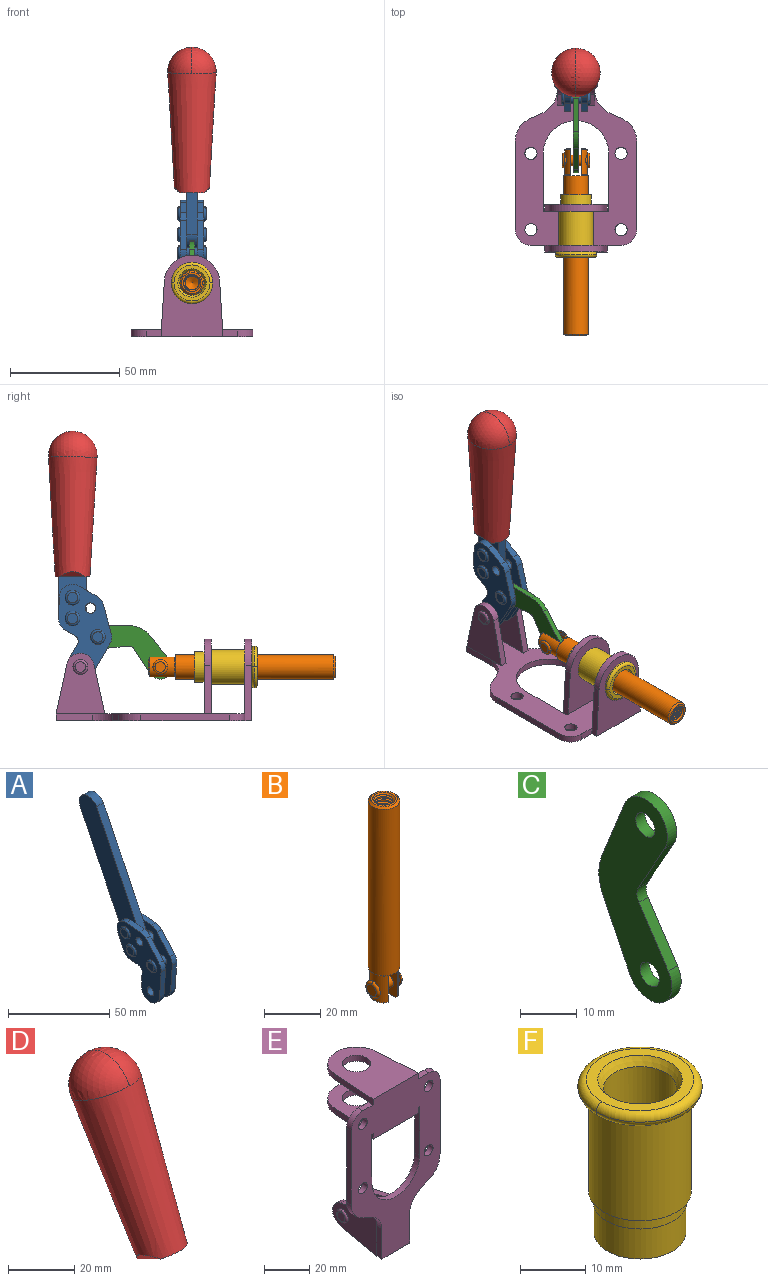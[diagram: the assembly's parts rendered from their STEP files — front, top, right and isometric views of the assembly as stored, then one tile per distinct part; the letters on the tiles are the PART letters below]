
ASSEMBLY  parts=6 mates=6
PART A: 59 faces, bbox 12.9x60.2x99.6 mm
  f0: torus R=2.39mm, axis (-1,0,0), area 14.9mm2, adj f20,f43,f51
  f1: torus R=2.39mm, axis (-1,0,0), area 14.9mm2, adj f19,f42,f51
  f2: torus R=2.39mm, axis (-1,0,0), area 14.9mm2, adj f18,f35,f51
  f3: torus R=2.39mm, axis (-1,0,0), area 14.9mm2, adj f14,f17,f23
  f4: torus R=2.39mm, axis (-1,0,0), area 14.9mm2, adj f13,f16,f23
  f5: torus R=2.39mm, axis (-1,0,0), area 14.9mm2, adj f12,f15,f23
  f6: cylinder r=2.39mm len=4.78mm, axis (1,0,0), area 46.5mm2, adj f48,f50,f51
  f7: cylinder r=2.39mm len=4.78mm, axis (1,0,0), area 46.5mm2, adj f50,f51
  f8: cylinder r=6.35mm len=12.68mm, axis (1,0,0), area 61.8mm2, adj f38,f39,f50,f51
  f9: cylinder r=2.39mm len=4.78mm, axis (-1,0,0), area 70.5mm2, adj f46,f50
  f10: cylinder r=2.39mm len=4.78mm, axis (-1,0,0), area 46.5mm2, adj f23,f45,f46
  f11: cylinder r=2.39mm len=4.78mm, axis (-1,0,0), area 46.5mm2, adj f23,f46
  f12: plane 4.78x4.78mm, normal (1,0,0), area 17.9mm2, adj f5,f15
  f13: plane 4.78x4.78mm, normal (1,0,0), area 17.9mm2, adj f4,f16
  f14: plane 4.78x4.78mm, normal (1,0,0), area 17.9mm2, adj f3,f17
  f15: torus R=2.39mm, axis (-1,0,0), area 14.9mm2, adj f5,f12,f23
  f16: torus R=2.39mm, axis (-1,0,0), area 14.9mm2, adj f4,f13,f23
  f17: torus R=2.39mm, axis (-1,0,0), area 14.9mm2, adj f3,f14,f23
  f18: plane 4.78x4.78mm, normal (-1,0,0), area 17.9mm2, adj f2,f35
  f19: plane 4.78x4.78mm, normal (-1,0,0), area 17.9mm2, adj f1,f42
  f20: plane 4.78x4.78mm, normal (-1,0,0), area 17.9mm2, adj f0,f43
  f21: plane 2.26x0.2mm, normal (1,0,0), area 0.2mm2, adj f31,f44
  f22: plane 2.26x0.2mm, normal (-1,0,0), area 0.2mm2, adj f41,f44
  f23: plane 39.37x30.77mm, normal (1,0,0), area 565.5mm2, adj f3,f4,f5,f10,f11,f15,f16,f17
  f24: cylinder r=6.1mm len=4.15mm, axis (-1,0,0), area 14.7mm2, adj f23,f25,f32,f46
  f25: plane 10.25x9.01mm, normal (0,-0.75,0.66), area 42.3mm2, adj f23,f24,f26,f46
  f26: cylinder r=6.35mm len=4.64mm, axis (-1,0,0), area 15.6mm2, adj f23,f25,f27,f46
  f27: plane 15.84x3.1mm, normal (0,-1,-0.07), area 49.2mm2, adj f23,f26,f28,f46
  f28: cylinder r=6.35mm len=12.68mm, axis (-1,0,0), area 61.8mm2, adj f23,f27,f29,f46
  f29: plane 8.11x3.1mm, normal (0,1,0.07), area 25.2mm2, adj f23,f28,f30,f46
  f30: cylinder r=3.05mm len=3.25mm, axis (-1,0,0), area 14.8mm2, adj f23,f29,f31,f46
  f31: plane 5.99x3.1mm, normal (0,0.07,-1), area 18.6mm2, adj f21,f23,f30,f44,f46
  f32: plane 9.5x3.1mm, normal (0,-0.07,1), area 29.5mm2, adj f23,f24,f33,f46,f47
  f33: cylinder r=6.1mm len=8.63mm, axis (-1,0,0), area 39.1mm2, adj f23,f32,f34,f47
  f34: plane 8.65x3.96mm, normal (0,0.91,-0.42), area 29.5mm2, adj f23,f33,f44,f47
  f35: torus R=2.39mm, axis (-1,0,0), area 14.9mm2, adj f2,f18,f51
  f36: plane 10.25x9.01mm, normal (0,-0.75,0.66), area 42.3mm2, adj f37,f49,f50,f51
  f37: cylinder r=6.35mm len=4.64mm, axis (1,0,0), area 15.6mm2, adj f36,f38,f50,f51
  f38: plane 15.84x3.1mm, normal (0,-1,-0.07), area 49.2mm2, adj f8,f37,f50,f51
  f39: plane 8.11x3.1mm, normal (0,1,0.07), area 25.2mm2, adj f8,f40,f50,f51
  f40: cylinder r=3.05mm len=3.25mm, axis (1,0,0), area 14.8mm2, adj f39,f41,f50,f51
  f41: plane 5.99x3.1mm, normal (0,0.07,-1), area 18.6mm2, adj f22,f40,f44,f50,f51
  f42: torus R=2.39mm, axis (-1,0,0), area 14.9mm2, adj f1,f19,f51
  f43: torus R=2.39mm, axis (-1,0,0), area 14.9mm2, adj f0,f20,f51
  f44: cylinder r=6.35mm len=12.12mm, axis (-1,0,0), area 128.9mm2, adj f21,f22,f23,f31,f34,f41,f46,f47
  f45: plane 2.65x1.35mm, normal (1,0,0), area 1mm2, adj f10,f55
  f46: plane 39.08x20.42mm, normal (-1,0,0), area 412.5mm2, adj f9,f10,f11,f24,f25,f26,f27,f28
  f47: plane 77.62x39.82mm, normal (1,0,0), area 850mm2, adj f32,f33,f34,f44,f53,f54,f55
  f48: plane 2.65x1.35mm, normal (-1,0,0), area 1mm2, adj f6,f55
  f49: cylinder r=6.1mm len=4.15mm, axis (1,0,0), area 14.7mm2, adj f36,f50,f51,f56
  f50: plane 39.08x20.42mm, normal (1,0,0), area 412.5mm2, adj f6,f7,f8,f9,f36,f37,f38,f39
  f51: plane 39.37x30.77mm, normal (-1,0,0), area 565.5mm2, adj f0,f1,f2,f6,f7,f8,f35,f36
  f52: plane 8.65x3.96mm, normal (0,0.91,-0.42), area 29.5mm2, adj f44,f51,f57,f58
  f53: plane 68.49x33.4mm, normal (0,0.9,-0.44), area 358.1mm2, adj f44,f47,f54,f58
  f54: cylinder r=6.35mm len=12.06mm, axis (1,0,0), area 93.7mm2, adj f47,f53,f55,f58
  f55: plane 68.49x33.4mm, normal (0,-0.9,0.44), area 358.1mm2, adj f44,f45,f46,f47,f48,f50,f54,f58
  f56: plane 9.5x3.1mm, normal (0,-0.07,1), area 29.5mm2, adj f49,f50,f51,f57,f58
  f57: cylinder r=6.1mm len=8.63mm, axis (1,0,0), area 39.1mm2, adj f51,f52,f56,f58
  f58: plane 77.62x39.82mm, normal (-1,0,0), area 850mm2, adj f44,f52,f53,f54,f55,f56,f57
PART B: 48 faces, bbox 12.6x11.1x86.1 mm
  f0: torus R=2.41mm, axis (-1,0,0), area 15mm2, adj f30,f32,f34
  f1: torus R=2.41mm, axis (-1,0,0), area 15mm2, adj f29,f31,f33
  f2: cylinder r=5.54mm len=72.39mm, axis (0,0,1), area 2518.5mm2, adj f3,f4,f42,f43
  f3: cone r=5.54mm half-angle=45deg, axis (0,0,1), area 7.6mm2, adj f2,f5,f41
  f4: cone r=5.54mm half-angle=45deg, axis (0,0,-1), area 34.9mm2, adj f2,f39
  f5: cylinder r=5.08mm len=11.48mm, axis (0,0,1), area 108.3mm2, adj f3,f7,f8,f41
  f6: cylinder r=2.41mm len=4.83mm, axis (-1,0,0), area 71.2mm2, adj f40,f41
  f7: cylinder r=2.41mm len=4.83mm, axis (-1,0,0), area 7.6mm2, adj f5,f34
  f8: cone r=5.08mm half-angle=45deg, axis (0,0,1), area 10.6mm2, adj f5,f37,f41
  f9: cone r=3.98mm half-angle=45deg, axis (0,0,1), area 17.6mm2, adj f27,f39,f45,f46,f47
  f10: cylinder r=2.41mm len=4.83mm, axis (-1,0,0), area 7.6mm2, adj f33,f38
  f11: cylinder r=3.2mm len=6.4mm, axis (0,0,1), area 78.4mm2, adj f12,f28,f44,f45,f47
  f12: cylinder r=3.2mm len=6.4mm, axis (0,0,1), area 10.5mm2, adj f11,f13,f45,f47
  f13: cylinder r=3.2mm len=6.4mm, axis (0,0,1), area 10.5mm2, adj f12,f14,f45,f47
  f14: cylinder r=3.2mm len=6.4mm, axis (0,0,1), area 10.5mm2, adj f13,f15,f45,f47
  f15: cylinder r=3.2mm len=6.4mm, axis (0,0,1), area 10.5mm2, adj f14,f16,f45,f47
  f16: cylinder r=3.2mm len=6.4mm, axis (0,0,1), area 10.5mm2, adj f15,f17,f45,f47
  f17: cylinder r=3.2mm len=6.4mm, axis (0,0,1), area 10.5mm2, adj f16,f18,f45,f47
  f18: cylinder r=3.2mm len=6.4mm, axis (0,0,1), area 10.5mm2, adj f17,f19,f45,f47
  f19: cylinder r=3.2mm len=6.4mm, axis (0,0,1), area 10.5mm2, adj f18,f20,f45,f47
  f20: cylinder r=3.2mm len=6.4mm, axis (0,0,1), area 10.5mm2, adj f19,f21,f45,f47
  f21: cylinder r=3.2mm len=6.4mm, axis (0,0,1), area 10.5mm2, adj f20,f22,f45,f47
  f22: cylinder r=3.2mm len=6.4mm, axis (0,0,1), area 10.5mm2, adj f21,f23,f45,f47
  f23: cylinder r=3.2mm len=6.4mm, axis (0,0,1), area 10.5mm2, adj f22,f24,f45,f47
  f24: cylinder r=3.2mm len=6.4mm, axis (0,0,1), area 10.5mm2, adj f23,f25,f45,f47
  f25: cylinder r=3.2mm len=6.4mm, axis (0,0,1), area 10.5mm2, adj f24,f26,f45,f47
  f26: cylinder r=3.2mm len=6.4mm, axis (0,0,1), area 10.5mm2, adj f25,f27,f45,f47
  f27: cylinder r=3.2mm len=6.4mm, axis (0,0,1), area 7.4mm2, adj f9,f26,f45,f47
  f28: cone r=3.2mm half-angle=60deg, axis (0,0,1), area 37.2mm2, adj f11
  f29: plane 4.83x4.83mm, normal (-1,0,0), area 18.3mm2, adj f1,f31
  f30: plane 4.83x4.83mm, normal (1,0,0), area 18.3mm2, adj f0,f32
  f31: torus R=2.41mm, axis (-1,0,0), area 15mm2, adj f1,f29,f33
  f32: torus R=2.41mm, axis (-1,0,0), area 15mm2, adj f0,f30,f34
  f33: plane 6.83x6.83mm, normal (1,0,0), area 18.3mm2, adj f1,f10,f31
  f34: plane 6.83x6.83mm, normal (-1,0,0), area 18.3mm2, adj f0,f7,f32
  f35: cone r=5.08mm half-angle=45deg, axis (0,0,1), area 10.6mm2, adj f36,f38,f40
  f36: plane 7.25x1.97mm, normal (0,0,-1), area 10mm2, adj f35,f40
  f37: plane 7.25x1.97mm, normal (0,0,-1), area 10mm2, adj f8,f41
  f38: cylinder r=5.08mm len=11.48mm, axis (0,0,1), area 108.3mm2, adj f10,f35,f40,f42
  f39: plane 9.55x9.55mm, normal (0,0,1), area 22mm2, adj f4,f9
  f40: plane 12.76x10.09mm, normal (1,0,0), area 95.7mm2, adj f6,f35,f36,f38,f42,f43
  f41: plane 12.76x10.09mm, normal (-1,0,0), area 95.7mm2, adj f3,f5,f6,f8,f37,f43
  f42: cone r=5.54mm half-angle=45deg, axis (0,0,1), area 7.6mm2, adj f2,f38,f40
  f43: plane 11.07x4.7mm, normal (0,0,-1), area 50.4mm2, adj f2,f40,f41
  f44: plane 0.89x0.62mm, normal (-1,0,0), area 0.3mm2, adj f11,f45,f46,f47
  f45: bspline ~24.8x7.63mm, area 266.6mm2, adj f9,f11,f12,f13,f14,f15,f16,f17
  f46: bspline ~24.87x7.63mm, area 73.6mm2, adj f9,f44,f45,f47
  f47: bspline ~24.98x7.63mm, area 272.5mm2, adj f9,f11,f12,f13,f14,f15,f16,f17
PART C: 12 faces, bbox 2.3x18.2x42.8 mm
  f0: cylinder r=2.4mm len=4.8mm, axis (1,0,0), area 34.9mm2, adj f4,f11
  f1: cylinder r=10.41mm len=8.47mm, axis (1,0,0), area 20.2mm2, adj f4,f9,f10,f11
  f2: cylinder r=3.05mm len=3.16mm, axis (1,0,0), area 7.7mm2, adj f4,f6,f7,f11
  f3: cylinder r=2.4mm len=4.8mm, axis (1,0,0), area 34.9mm2, adj f4,f11
  f4: plane 42.81x18.23mm, normal (-1,0,0), area 414.1mm2, adj f0,f1,f2,f3,f5,f6,f7,f8
  f5: cylinder r=5.54mm len=10.67mm, axis (1,0,0), area 41.8mm2, adj f4,f6,f10,f11
  f6: plane 11.66x6.53mm, normal (0,-0.87,-0.49), area 30.9mm2, adj f2,f4,f5,f11
  f7: plane 11.17x7.33mm, normal (0,-0.84,0.55), area 30.9mm2, adj f2,f4,f8,f11
  f8: cylinder r=5.54mm len=10.51mm, axis (1,0,0), area 41.8mm2, adj f4,f7,f9,f11
  f9: plane 13.67x6.67mm, normal (0,0.9,-0.44), area 35.1mm2, adj f1,f4,f8,f11
  f10: plane 14.1x5.7mm, normal (0,0.93,0.37), area 35.1mm2, adj f1,f4,f5,f11
  f11: plane 42.81x18.23mm, normal (1,0,0), area 414.1mm2, adj f0,f1,f2,f3,f5,f6,f7,f8
PART D: 11 faces, bbox 22.3x42.6x64.5 mm
  f0: sphere r=11.13mm, area 411.4mm2, adj f1,f8
  f1: cone r=11.11mm half-angle=3.3deg, axis (0,0.44,0.9), area 3251.8mm2, adj f0,f7,f8,f9,f10
  f2: cylinder r=6.16mm len=11.7mm, axis (1,0,0), area 89.5mm2, adj f3,f4,f5,f6
  f3: plane 60.23x36.75mm, normal (-1,0,0), area 763.6mm2, adj f2,f4,f6,f10
  f4: plane 51.37x25.05mm, normal (0,0.9,-0.44), area 264.2mm2, adj f2,f3,f5,f10
  f5: plane 60.23x36.75mm, normal (1,0,0), area 763.6mm2, adj f2,f4,f6,f10
  f6: plane 51.37x25.05mm, normal (0,-0.9,0.44), area 264.2mm2, adj f2,f3,f5,f10
  f7: plane 9.95x5.95mm, normal (0.71,-0.31,-0.64), area 25.8mm2, adj f1,f10
  f8: sphere r=11.13mm, area 411.4mm2, adj f0,f1
  f9: plane 9.95x5.95mm, normal (-0.71,-0.31,-0.64), area 25.8mm2, adj f1,f10
  f10: plane 14.27x11.38mm, normal (0,-0.44,-0.9), area 106.7mm2, adj f1,f3,f4,f5,f6,f7,f9
PART E: 55 faces, bbox 55.7x37.4x89.8 mm
  f0: torus R=2.41mm, axis (-1,0,0), area 15mm2, adj f11,f15,f25
  f1: torus R=2.41mm, axis (-1,0,0), area 15mm2, adj f10,f12,f22
  f2: cylinder r=2.78mm len=5.56mm, axis (0,-1,0), area 54.2mm2, adj f30,f54
  f3: cylinder r=14.99mm len=29.97mm, axis (0,-1,0), area 145.9mm2, adj f30,f49,f53,f54
  f4: cylinder r=2.78mm len=5.56mm, axis (0,-1,0), area 54.2mm2, adj f30,f54
  f5: cylinder r=2.78mm len=5.56mm, axis (0,-1,0), area 54.2mm2, adj f30,f54
  f6: cylinder r=2.78mm len=5.56mm, axis (0,-1,0), area 54.2mm2, adj f30,f54
  f7: cylinder r=6.35mm len=12.7mm, axis (0,0,1), area 123.6mm2, adj f27,f51
  f8: cylinder r=6.35mm len=12.7mm, axis (0,0,-1), area 124.7mm2, adj f21,f35
  f9: cylinder r=2.41mm len=11.18mm, axis (-1,0,0), area 169.4mm2, adj f16,f19
  f10: plane 4.83x4.83mm, normal (1,0,0), area 18.3mm2, adj f1,f12
  f11: plane 4.83x4.83mm, normal (-1,0,0), area 18.3mm2, adj f0,f15
  f12: torus R=2.41mm, axis (-1,0,0), area 15mm2, adj f1,f10,f22
  f13: cylinder r=6.35mm len=12.41mm, axis (1,0,0), area 53.4mm2, adj f18,f19,f22,f23
  f14: cylinder r=6.35mm len=12.41mm, axis (-1,0,0), area 53.4mm2, adj f16,f17,f24,f25
  f15: torus R=2.41mm, axis (-1,0,0), area 15mm2, adj f0,f11,f25
  f16: plane 27.86x22.35mm, normal (1,0,0), area 425.4mm2, adj f9,f14,f17,f24,f30
  f17: plane 22.86x4.97mm, normal (0,0.21,0.98), area 72.5mm2, adj f14,f16,f25,f30
  f18: plane 22.86x4.97mm, normal (0,0.21,0.98), area 72.5mm2, adj f13,f19,f22,f30
  f19: plane 27.86x22.35mm, normal (-1,0,0), area 425.4mm2, adj f9,f13,f18,f23,f30
  f20: cylinder r=12.7mm len=25.35mm, axis (0,0,-1), area 119.8mm2, adj f21,f34,f35,f36
  f21: plane 34.21x28.07mm, normal (0,0,-1), area 702.4mm2, adj f8,f20,f30,f34,f36
  f22: plane 27.96x22.45mm, normal (1,0,0), area 407.2mm2, adj f1,f12,f13,f18,f23,f30,f42,f43
  f23: plane 22.86x4.97mm, normal (0,0.21,-0.98), area 72.5mm2, adj f13,f19,f22,f44
  f24: plane 22.86x4.97mm, normal (0,0.21,-0.98), area 72.5mm2, adj f14,f16,f25,f44
  f25: plane 27.86x22.35mm, normal (-1,0,0), area 407.1mm2, adj f0,f14,f15,f17,f24,f30,f45,f46
  f26: plane 3.1x0.95mm, normal (0,0,-1), area 2.7mm2, adj f30,f49,f50,f54
  f27: plane 34.21x28.07mm, normal (0,0,1), area 702.4mm2, adj f7,f28,f30,f50,f52
  f28: cylinder r=12.7mm len=25.35mm, axis (0,0,1), area 118.8mm2, adj f27,f50,f51,f52
  f29: plane 3.1x0.95mm, normal (0,0,-1), area 2.7mm2, adj f30,f52,f53,f54
  f30: plane 86.54x55.63mm, normal (0,1,0), area 2362.9mm2, adj f2,f3,f4,f5,f6,f16,f17,f18
  f31: plane 40.56x3.1mm, normal (-1,0,0), area 125.7mm2, adj f30,f32,f48,f54
  f32: cylinder r=7.11mm len=7.11mm, axis (0,-1,0), area 34.6mm2, adj f30,f31,f33,f54
  f33: plane 6.67x3.1mm, normal (0,0,1), area 20.4mm2, adj f30,f32,f34,f54
  f34: plane 25.39x3.13mm, normal (-1,0.06,0), area 79.5mm2, adj f20,f21,f33,f35,f54
  f35: plane 37.31x28.45mm, normal (0,0,1), area 789.9mm2, adj f8,f20,f34,f36,f54
  f36: plane 25.39x3.13mm, normal (1,0.06,0), area 79.5mm2, adj f20,f21,f35,f37,f54
  f37: plane 6.67x3.1mm, normal (0,0,1), area 20.4mm2, adj f30,f36,f38,f54
  f38: cylinder r=7.11mm len=7.11mm, axis (0,-1,0), area 34.6mm2, adj f30,f37,f39,f54
  f39: plane 40.56x3.1mm, normal (1,0,0), area 125.7mm2, adj f30,f38,f40,f54
  f40: cylinder r=11.18mm len=10.16mm, axis (0,-1,0), area 39.5mm2, adj f30,f39,f41,f54
  f41: plane 6.09x3.1mm, normal (0.42,0,-0.91), area 20.8mm2, adj f30,f40,f42,f54
  f42: cylinder r=11.18mm len=9.41mm, axis (0,-1,0), area 37.2mm2, adj f22,f30,f41,f43,f54
  f43: plane 16.5x3.1mm, normal (1,0,0), area 51.1mm2, adj f22,f42,f44,f54
  f44: plane 17.37x3.1mm, normal (0,0,-1), area 53.8mm2, adj f23,f24,f30,f43,f45,f54
  f45: plane 16.5x3.1mm, normal (-1,0,0), area 51.1mm2, adj f25,f44,f46,f54
  f46: cylinder r=11.18mm len=9.41mm, axis (0,-1,0), area 37.2mm2, adj f25,f30,f45,f47,f54
  f47: plane 6.09x3.1mm, normal (-0.42,0,-0.91), area 20.8mm2, adj f30,f46,f48,f54
  f48: cylinder r=11.18mm len=10.16mm, axis (0,-1,0), area 39.5mm2, adj f30,f31,f47,f54
  f49: plane 26.54x3.1mm, normal (-1,0,0), area 82.3mm2, adj f3,f26,f30,f54
  f50: plane 25.39x3.1mm, normal (1,0.06,0), area 78.8mm2, adj f26,f27,f28,f51,f54
  f51: plane 37.31x28.45mm, normal (0,0,-1), area 789.9mm2, adj f7,f28,f50,f52,f54
  f52: plane 25.39x3.1mm, normal (-1,0.06,0), area 78.8mm2, adj f27,f28,f29,f51,f54
  f53: plane 26.54x3.1mm, normal (1,0,0), area 82.3mm2, adj f3,f29,f30,f54
  f54: plane 89.66x55.63mm, normal (0,-1,0), area 2678.5mm2, adj f2,f3,f4,f5,f6,f26,f29,f31
PART F: 15 faces, bbox 20.6x20.6x28.7 mm
  f0: torus R=8.26mm, axis (0,0,1), area 56.8mm2, adj f1,f10,f12
  f1: torus R=8.26mm, axis (0,0,1), area 56.8mm2, adj f0,f6,f13
  f2: cylinder r=5.59mm len=25.91mm, axis (0,0,1), area 909.6mm2, adj f3,f4
  f3: cone r=6.86mm half-angle=45deg, axis (0,0,-1), area 70.2mm2, adj f2,f14
  f4: cone r=6.47mm half-angle=30deg, axis (0,0,1), area 66.7mm2, adj f2,f13
  f5: cylinder r=7.04mm len=14.07mm, axis (0,0,1), area 252.6mm2, adj f11,f14
  f6: torus R=8.26mm, axis (0,0,1), area 56.8mm2, adj f1,f12,f13
  f7: cylinder r=7.16mm len=14.33mm, axis (0,0,1), area 91.5mm2, adj f9,f11
  f8: cylinder r=7.86mm len=18.42mm, axis (0,0,1), area 909.6mm2, adj f9,f10
  f9: plane 15.72x15.72mm, normal (0,0,-1), area 33mm2, adj f7,f8
  f10: plane 16.51x16.51mm, normal (0,0,-1), area 19.9mm2, adj f0,f8,f12
  f11: plane 14.33x14.33mm, normal (0,0,-1), area 5.7mm2, adj f5,f7
  f12: torus R=8.26mm, axis (0,0,1), area 56.8mm2, adj f0,f6,f10
  f13: plane 16.51x16.51mm, normal (0,0,1), area 82.7mm2, adj f1,f4,f6
  f14: plane 14.07x14.07mm, normal (0,0,-1), area 7.8mm2, adj f3,f5
PLACE A rot(axis=(1,0,0),26.1deg) t=(0,5.31,42.61)mm
PLACE B rot(axis=(1,0,0),90deg) t=(0,20.41,0)mm
PLACE C rot(axis=(0,-0.55,-0.84),180deg) t=(0,29.26,9.6)mm
PLACE D rot(axis=(1,0,0),26.1deg) t=(-0.04,5.31,42.61)mm
PLACE E rot(axis=(1,0,0),90deg) t=(0,9.43,0)mm fixed
PLACE F rot(axis=(1,0,0),90deg) t=(0,9.43,0)mm
MATE revolute C.f5 <-> A.f4  axis (-1,0,0) through (0,33.56,38.35)mm
MATE fastened F.f0 <-> E.f7  axis (0,1,0) through (0,-36.96,24.61)mm
MATE fastened D.f2 <-> A.f54  axis (1,0,0) through (-2.35,45.02,123.05)mm
MATE slider B.f2 <-> E.f7  axis (0,-1,0) through (0,-38.37,24.61)mm
MATE revolute C.f3 <-> B.f6  axis (-1,0,0) through (0,4.94,24.61)mm
MATE revolute A.f7 <-> E.f0  axis (1,0,0) through (0,41.52,24.61)mm
